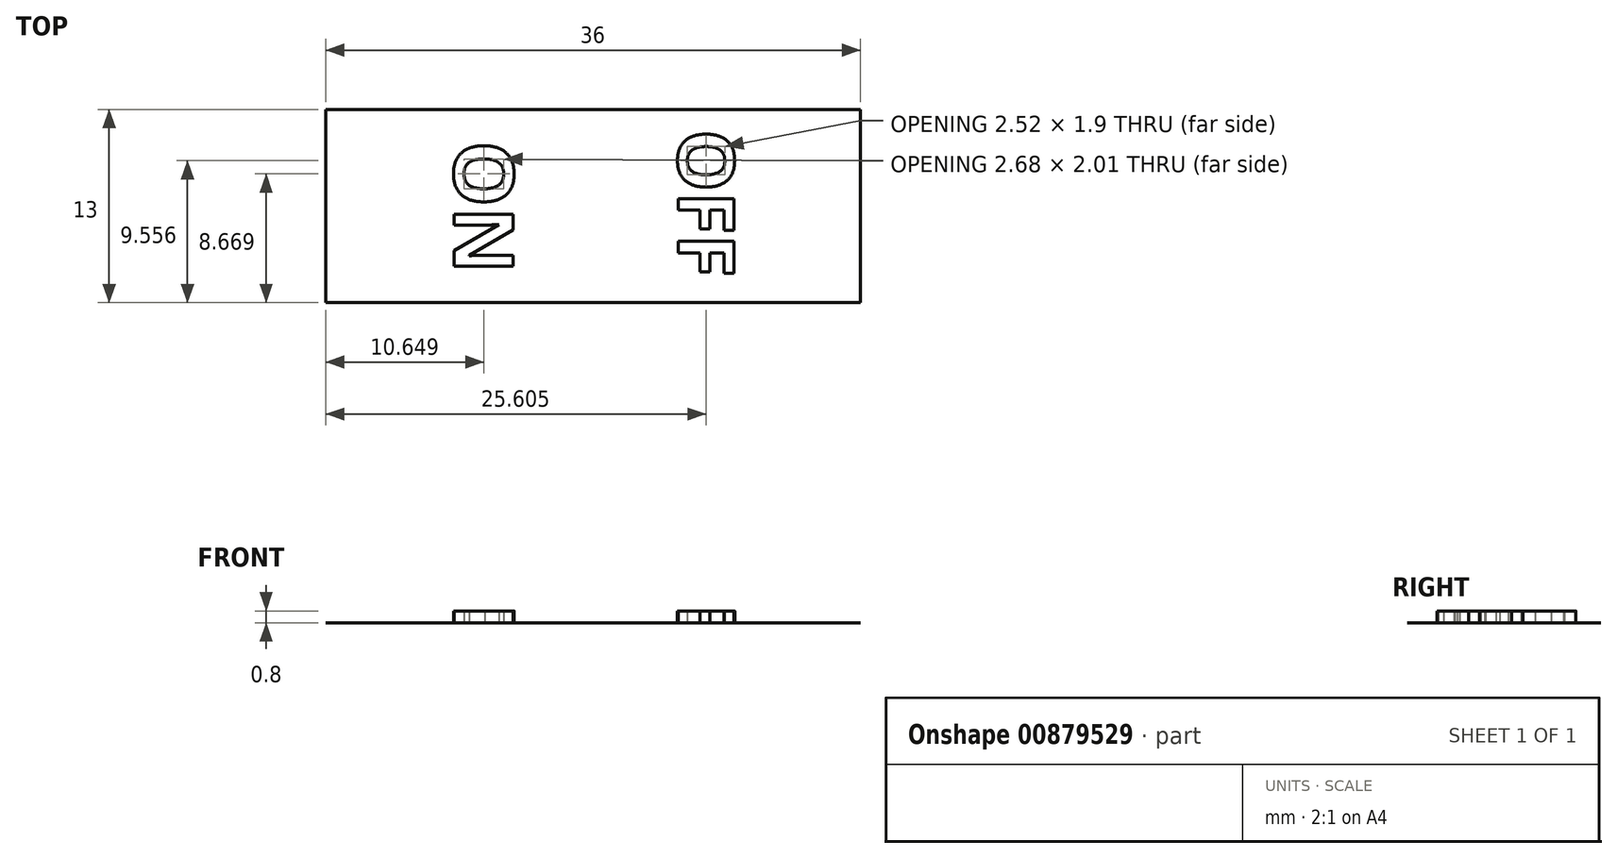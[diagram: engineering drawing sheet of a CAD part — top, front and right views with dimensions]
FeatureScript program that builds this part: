
annotation { "Feature Type Name" : "Feature", "Feature Type Description" : "" }
export const myFeature = defineFeature(function(context is Context, id is Id, definition is map)
    precondition{}
    {
        {
            var Q0;
            Q0=qCreatedBy(makeId("Top.planeOp"),FACE);
            var sketch = newSketch(context, id + "F0", { "sketchPlane" : qUnion([Q0])});
            skLineSegment(sketch, "E0.bottom", {"start": v(10, -6.5) * mm, "end": v(-10, -6.5) * mm});
            skLineSegment(sketch, "E0.top", {"start": v(10, 6.5) * mm, "end": v(-10, 6.5) * mm});
            skLineSegment(sketch, "E0.left", {"start": v(10, -6.5) * mm, "end": v(10, 6.5) * mm});
            skLineSegment(sketch, "E0.right", {"start": v(-10, -6.5) * mm, "end": v(-10, 6.5) * mm});
            skPoint(sketch, "E0.middle", {"position": v(0, 0) * mm});
            skLineSegment(sketch, "E1.bottom", {"start": v(6.9, -4.3) * mm, "end": v(-6.9, -4.3) * mm});
            skLineSegment(sketch, "E1.top", {"start": v(6.9, 4.3) * mm, "end": v(-6.9, 4.3) * mm});
            skLineSegment(sketch, "E1.left", {"start": v(6.9, -4.3) * mm, "end": v(6.9, 4.3) * mm});
            skLineSegment(sketch, "E1.right", {"start": v(-6.9, -4.3) * mm, "end": v(-6.9, 4.3) * mm});
            skSolve(sketch);
        }
        {
            var Q0;
            Q0=makeQuery(id+"F0.imprint","IMPRINT",FACE,{"disambiguationData":[TD([[makeQuery(id+"F0.imprint","IMPRINT",EDGE,{"derivedFrom":sQuery(id+"F0.wireOp",EDGE,"E0.bottom")}),-1.0]])]});
            extrude(context, id + "F1", {"entities" : qUnion([Q0]), "depth" : 16 * mm, "offsetDistance" : 25 * mm});
        }
        {
            var Q0;
            Q0=makeQuery(id+"F1.opExtrude","CAP_FACE",FACE,{"disambiguationData":[OSD([sQuery(id+"F0.wireOp",EDGE,"E0.bottom"),sQuery(id+"F0.wireOp",EDGE,"E0.top"),sQuery(id+"F0.wireOp",EDGE,"E0.left"),sQuery(id+"F0.wireOp",EDGE,"E0.right"),sQuery(id+"F0.wireOp",EDGE,"E1.bottom"),sQuery(id+"F0.wireOp",EDGE,"E1.top"),sQuery(id+"F0.wireOp",EDGE,"E1.left"),sQuery(id+"F0.wireOp",EDGE,"E1.right")])],"isStart":true});
            var sketch = newSketch(context, id + "F2", { "sketchPlane" : qUnion([Q0])});
            skLineSegment(sketch, "E2.bottom", {"start": v(18, -6.5) * mm, "end": v(-18, -6.5) * mm});
            skLineSegment(sketch, "E2.top", {"start": v(18, 6.5) * mm, "end": v(-18, 6.5) * mm});
            skLineSegment(sketch, "E2.left", {"start": v(18, -6.5) * mm, "end": v(18, 6.5) * mm});
            skLineSegment(sketch, "E2.right", {"start": v(-18, -6.5) * mm, "end": v(-18, 6.5) * mm});
            skPoint(sketch, "E2.middle", {"position": v(0, 0) * mm});
            skSolve(sketch);
        }
        {
            var Q0;
            Q0=qSketchRegion(id+"F2",true);
            extrude(context, id + "F3", {"entities" : qUnion([Q0]), "operationType" : NewBodyOperationType.ADD, "depth" : 2 * mm, "offsetDistance" : 25 * mm});
        }
        {
            var Q0;
            Q0=makeQuery(id+"F1.opExtrude","CAP_FACE",FACE,{"disambiguationData":[OSD([sQuery(id+"F0.wireOp",EDGE,"E0.bottom"),sQuery(id+"F0.wireOp",EDGE,"E0.top"),sQuery(id+"F0.wireOp",EDGE,"E0.left"),sQuery(id+"F0.wireOp",EDGE,"E0.right"),sQuery(id+"F0.wireOp",EDGE,"E1.bottom"),sQuery(id+"F0.wireOp",EDGE,"E1.top"),sQuery(id+"F0.wireOp",EDGE,"E1.left"),sQuery(id+"F0.wireOp",EDGE,"E1.right")])],"isStart":false});
            var sketch = newSketch(context, id + "F4", { "sketchPlane" : qUnion([Q0])});
            skLineSegment(sketch, "E3.bottom", {"start": v(-10, 6.5) * mm, "end": v(10, 6.5) * mm});
            skLineSegment(sketch, "E3.top", {"start": v(-10, -6.5) * mm, "end": v(10, -6.5) * mm});
            skLineSegment(sketch, "E3.left", {"start": v(-10, 6.5) * mm, "end": v(-10, -6.5) * mm});
            skLineSegment(sketch, "E3.right", {"start": v(10, 6.5) * mm, "end": v(10, -6.5) * mm});
            skSolve(sketch);
        }
        {
            var Q0;
            Q0=makeQuery(id+"F1.opExtrude","CAP_EDGE",EDGE,{"disambiguationData":[OSD([sQuery(id+"F0.wireOp",EDGE,"E1.left")])],"isStart":true});
            var Q1;
            Q1=makeQuery(id+"F1.opExtrude","CAP_EDGE",EDGE,{"disambiguationData":[OSD([sQuery(id+"F0.wireOp",EDGE,"E1.left")])],"isStart":false});
            cPlane(context, id + "F5", {"entities" : qUnion([Q0, Q1]), "cplaneType" : CPlaneType.LINE_ANGLE, "offset" : 25 * mm, "angle" : 0 * degree, "width" : 150 * mm, "height" : 150 * mm});
        }
        {
            var Q0;
            Q0=qCreatedBy(id+"F5.planeOp",FACE);
            var sketch = newSketch(context, id + "F6", { "sketchPlane" : qUnion([Q0])});
            skLineSegment(sketch, "E4.bottom", {"start": v(-4.3, 2) * mm, "end": v(4.3, 2) * mm});
            skLineSegment(sketch, "E4.top", {"start": v(-4.3, 16) * mm, "end": v(4.3, 16) * mm});
            skLineSegment(sketch, "E4.left", {"start": v(-4.3, 2) * mm, "end": v(-4.3, 16) * mm});
            skLineSegment(sketch, "E4.right", {"start": v(4.3, 2) * mm, "end": v(4.3, 16) * mm});
            skPoint(sketch, "E5", {"position": v(-4.3, 2) * mm});
            skPoint(sketch, "E6", {"position": v(-4.3, 0) * mm});
            skSolve(sketch);
        }
        {
            var Q0;
            Q0=qSketchRegion(id+"F6",true);
            var Q1;
            Q1=makeQuery(id+"F1.opExtrude","SWEPT_FACE",FACE,{"disambiguationData":[OSD([sQuery(id+"F0.wireOp",EDGE,"E0.left")])]});
            extrude(context, id + "F7", {"entities" : qUnion([Q0]), "operationType" : NewBodyOperationType.REMOVE, "endBound" : BoundingType.UP_TO_SURFACE, "depth" : 25 * mm, "endBoundEntityFace" : qUnion([Q1]), "offsetDistance" : 25 * mm});
        }
        {
            var Q0;
            Q0=makeQuery(id+"F4.imprint","IMPRINT",FACE,{"disambiguationData":[TD([[makeQuery(id+"F4.imprint","IMPRINT",EDGE,{"derivedFrom":sQuery(id+"F4.wireOp",EDGE,"E3.bottom")}),1.0]])]});
            var sketch = newSketch(context, id + "F8", { "sketchPlane" : qUnion([Q0])});
            skLineSegment(sketch, "E7.bottom", {"start": v(-10, 6.5) * mm, "end": v(10, 6.5) * mm});
            skLineSegment(sketch, "E7.top", {"start": v(-10, -6.5) * mm, "end": v(10, -6.5) * mm});
            skLineSegment(sketch, "E7.left", {"start": v(-10, 6.5) * mm, "end": v(-10, -6.5) * mm});
            skLineSegment(sketch, "E7.right", {"start": v(10, 6.5) * mm, "end": v(10, -6.5) * mm});
            skSolve(sketch);
        }
        {
            var Q0;
            Q0=qSketchRegion(id+"F8",true);
            extrude(context, id + "F9", {"entities" : qUnion([Q0]), "operationType" : NewBodyOperationType.ADD, "depth" : 2 * mm, "offsetDistance" : 25 * mm});
        }
        {
            var Q0;
            Q0=makeQuery(id+"F9.opExtrude","CAP_FACE",FACE,{"disambiguationData":[OSD([sQuery(id+"F8.wireOp",EDGE,"E7.bottom"),sQuery(id+"F8.wireOp",EDGE,"E7.top"),sQuery(id+"F8.wireOp",EDGE,"E7.left"),sQuery(id+"F8.wireOp",EDGE,"E7.right")])],"isStart":false});
            var sketch = newSketch(context, id + "F10", { "sketchPlane" : qUnion([Q0])});
            skPoint(sketch, "E8", {"position": v(0, 0) * mm});
            skCircle(sketch, "E9", {"center": v(0, 0) * mm, "radius": 3.5 * mm});
            skSolve(sketch);
        }
        {
            var Q0;
            Q0=qSketchRegion(id+"F10",true);
            var Q1;
            Q1=makeQuery(id+"F9.opExtrude","CAP_FACE",FACE,{"disambiguationData":[OSD([sQuery(id+"F8.wireOp",EDGE,"E7.bottom"),sQuery(id+"F8.wireOp",EDGE,"E7.top"),sQuery(id+"F8.wireOp",EDGE,"E7.left"),sQuery(id+"F8.wireOp",EDGE,"E7.right")])],"isStart":true});
            extrude(context, id + "F11", {"entities" : qUnion([Q0]), "operationType" : NewBodyOperationType.REMOVE, "endBound" : BoundingType.UP_TO_SURFACE, "oppositeDirection" : true, "depth" : 25 * mm, "endBoundEntityFace" : qUnion([Q1]), "offsetDistance" : 25 * mm});
        }
        {
            var Q0;
            {var subQ0=sQuery(id+"F2.wireOp",EDGE,"E2.top");var subQ1=sQuery(id+"F2.wireOp",EDGE,"E2.bottom");var subQ2=sQuery(id+"F2.wireOp",EDGE,"E2.left");Q0=makeQuery(id+"F3.boolean.opBoolean","SPLIT",FACE,{"disambiguationData":[TD([makeQuery(id+"F1.opExtrude","SWEPT_FACE",FACE,{"disambiguationData":[OSD([sQuery(id+"F0.wireOp",EDGE,"E0.left")])]})])],"derivedFrom":makeQuery(id+"F3.opExtrude","CAP_FACE",FACE,{"disambiguationData":[OSD([subQ1,subQ0,subQ2,sQuery(id+"F2.wireOp",EDGE,"E2.right")])],"isStart":true})});}
            var sketch = newSketch(context, id + "F12", { "sketchPlane" : qUnion([Q0])});
            skPoint(sketch, "E10", {"position": v(14, 0) * mm});
            skPoint(sketch, "E10.positionSnap0", {"position": v(14, 6.5) * mm});
            skPoint(sketch, "E10.positionSnap1", {"position": v(18, 0) * mm});
            skPoint(sketch, "E11", {"position": v(-14, 0) * mm});
            skPoint(sketch, "E12", {"position": v(-14, 6.5) * mm});
            skCircle(sketch, "E13", {"center": v(14, 0) * mm, "radius": 2 * mm});
            skCircle(sketch, "E14", {"center": v(-14, 0) * mm, "radius": 2 * mm});
            skSolve(sketch);
        }
        {
            var Q0;
            Q0=makeQuery(id+"F12.imprint","IMPRINT",FACE,{"disambiguationData":[TD([[makeQuery(id+"F12.imprint","IMPRINT",EDGE,{"derivedFrom":sQuery(id+"F12.wireOp",EDGE,"E13")}),1.0]])]});
            var Q1;
            Q1=makeQuery(id+"F12.imprint","IMPRINT",FACE,{"disambiguationData":[TD([[makeQuery(id+"F12.imprint","IMPRINT",EDGE,{"derivedFrom":sQuery(id+"F12.wireOp",EDGE,"E14")}),1.0]])]});
            var Q2;
            Q2=makeQuery(id+"F3.opExtrude","CAP_FACE",FACE,{"disambiguationData":[OSD([sQuery(id+"F2.wireOp",EDGE,"E2.bottom"),sQuery(id+"F2.wireOp",EDGE,"E2.top"),sQuery(id+"F2.wireOp",EDGE,"E2.left"),sQuery(id+"F2.wireOp",EDGE,"E2.right")])],"isStart":false});
            extrude(context, id + "F13", {"entities" : qUnion([Q0, Q1]), "operationType" : NewBodyOperationType.REMOVE, "endBound" : BoundingType.UP_TO_SURFACE, "oppositeDirection" : true, "depth" : 25 * mm, "endBoundEntityFace" : qUnion([Q2]), "offsetDistance" : 25 * mm});
        }
        {
            var Q0;
            Q0=makeQuery(id+"F9.opExtrude","CAP_FACE",FACE,{"disambiguationData":[OSD([sQuery(id+"F8.wireOp",EDGE,"E7.bottom"),sQuery(id+"F8.wireOp",EDGE,"E7.top"),sQuery(id+"F8.wireOp",EDGE,"E7.left"),sQuery(id+"F8.wireOp",EDGE,"E7.right")])],"isStart":false});
            var sketch = newSketch(context, id + "F14", { "sketchPlane" : qUnion([Q0])});
            skText(sketch, "E15", { "text": "ON", "fontName": "OpenSans-Bold.ttf"});
            skText(sketch, "E16", { "text": "OFF\n", "fontName": "OpenSans-Bold.ttf"});
            skLineSegment(sketch, "E17.bottom", {"start": v(18, 6.5) * mm, "end": v(-18, 6.5) * mm, "construction": true});
            skLineSegment(sketch, "E17.top", {"start": v(18, -6.5) * mm, "end": v(-18, -6.5) * mm, "construction": true});
            skLineSegment(sketch, "E17.left", {"start": v(18, 6.5) * mm, "end": v(18, -6.5) * mm, "construction": true});
            skLineSegment(sketch, "E17.right", {"start": v(-18, 6.5) * mm, "end": v(-18, -6.5) * mm, "construction": true});
            const initialGuessF14  = {"E15": [-0.00934, 0.00438, 0, -1, 0.004], "E16": [0.00573, 0.00514, 0, -1, 0.00377]};
            skSetInitialGuess(sketch, initialGuessF14);
            skSolve(sketch);
        }
        {
            var Q0;
            Q0 = qSketchRegion(id + "F14", true);
            extrude(context, id + "F15", {"entities" : qUnion([Q0]), "operationType" : NewBodyOperationType.ADD, "depth" : .8 * mm, "offsetDistance" : 25 * mm});
        }
        {
            var Q0;
            {var subQ0=sQuery(id+"F8.wireOp",EDGE,"E7.right");var subQ1=sQuery(id+"F8.wireOp",EDGE,"E7.left");var subQ2=sQuery(id+"F8.wireOp",EDGE,"E7.top");var subQ3=sQuery(id+"F8.wireOp",EDGE,"E7.bottom");Q0=makeQuery(id+"F15.boolean.opBoolean","SPLIT",FACE,{"disambiguationData":[TD([makeQuery(id+"F1.opExtrude","SWEPT_FACE",FACE,{"disambiguationData":[OSD([sQuery(id+"F0.wireOp",EDGE,"E0.bottom")])]})])],"derivedFrom":makeQuery(id+"F9.opExtrude","CAP_FACE",FACE,{"disambiguationData":[OSD([subQ3,subQ2,subQ1,subQ0])],"isStart":false})});}
            var sketch = newSketch(context, id + "F16", { "sketchPlane" : qUnion([Q0])});
            skLineSegment(sketch, "E18.bottom", {"start": v(18, 6.5) * mm, "end": v(-18, 6.5) * mm});
            skLineSegment(sketch, "E18.top", {"start": v(18, -6.5) * mm, "end": v(-18, -6.5) * mm});
            skLineSegment(sketch, "E18.left", {"start": v(18, 6.5) * mm, "end": v(18, -6.5) * mm});
            skLineSegment(sketch, "E18.right", {"start": v(-18, 6.5) * mm, "end": v(-18, -6.5) * mm});
            skSolve(sketch);
        }
        {
            var Q0;
            Q0 = qSketchRegion(id + "F16", true);
            extrude(context, id + "F17", {"entities" : qUnion([Q0]), "operationType" : NewBodyOperationType.ADD, "depth" : 0 * mm, "offsetDistance" : 25 * mm});
        }
        {
            var Q0;
            Q0=makeQuery(id+"F17.boolean.opBoolean","MERGE",FACE,{"derivedFrom":[makeQuery(id+"F9.boolean.opBoolean","MERGE",FACE,{"derivedFrom":[makeQuery(id+"F3.boolean.opBoolean","MERGE",FACE,{"derivedFrom":[makeQuery(id+"F1.opExtrude","SWEPT_FACE",FACE,{"disambiguationData":[OSD([sQuery(id+"F0.wireOp",EDGE,"E0.top")])]}),makeQuery(id+"F3.opExtrude","SWEPT_FACE",FACE,{"disambiguationData":[OSD([sQuery(id+"F2.wireOp",EDGE,"E2.bottom")])]})]}),makeQuery(id+"F9.opExtrude","SWEPT_FACE",FACE,{"disambiguationData":[OSD([sQuery(id+"F8.wireOp",EDGE,"E7.bottom")])]})]}),makeQuery(id+"F17.opExtrude","SWEPT_FACE",FACE,{"disambiguationData":[OSD([sQuery(id+"F16.wireOp",EDGE,"E18.bottom")])]})]});
            var sketch = newSketch(context, id + "F18", { "sketchPlane" : qUnion([Q0])});
            skLineSegment(sketch, "E19.bottom", {"start": v(-18, -2) * mm, "end": v(26.02, -2) * mm});
            skLineSegment(sketch, "E19.top", {"start": v(-18, 18) * mm, "end": v(26.02, 18) * mm});
            skLineSegment(sketch, "E19.left", {"start": v(-18, -2) * mm, "end": v(-18, 18) * mm});
            skLineSegment(sketch, "E19.right", {"start": v(26.02, -2) * mm, "end": v(26.02, 18) * mm});
            skSolve(sketch);
        }
        {
            var Q0;
            Q0 = qSketchRegion(id + "F18", true);
            extrude(context, id + "F19", {"entities" : qUnion([Q0]), "operationType" : NewBodyOperationType.REMOVE, "oppositeDirection" : true, "depth" : 25 * mm, "offsetDistance" : 25 * mm});
        }
    });
